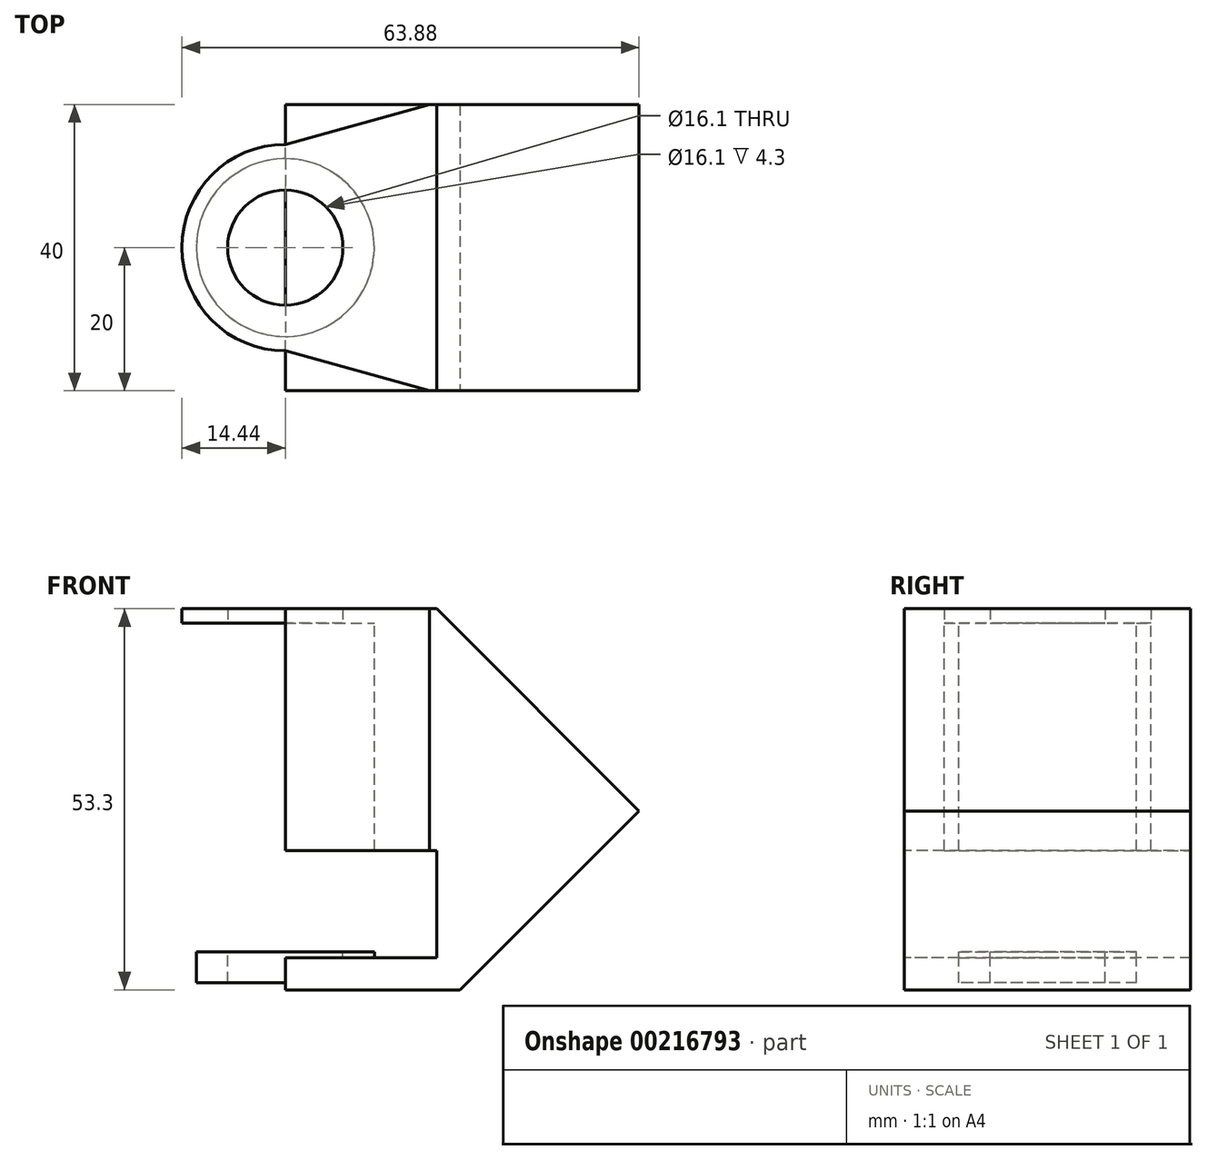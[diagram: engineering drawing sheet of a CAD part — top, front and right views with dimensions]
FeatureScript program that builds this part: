
annotation { "Feature Type Name" : "Feature", "Feature Type Description" : "" }
export const myFeature = defineFeature(function(context is Context, id is Id, definition is map)
    precondition{}
    {
        {
            var Q0;
            Q0=qCreatedBy(makeId("Top.planeOp"),FACE);
            var sketch = newSketch(context, id + "F0", { "sketchPlane" : qUnion([Q0])});
            skCircle(sketch, "E0", {"center": v(0, 0) * mm, "radius": 12.44 * mm});
            skCircle(sketch, "E1", {"center": v(0, 0) * mm, "radius": 8.05 * mm});
            skLineSegment(sketch, "E2", {"start": v(20.16, 20) * mm, "end": v(20.16, -20) * mm});
            skPoint(sketch, "E3", {"position": v(20.16, 0) * mm});
            skCircle(sketch, "E4.0", {"center": v(0, 0) * mm, "radius": 14.44 * mm});
            skFitSpline(sketch, "E5", {"points": [v(0, 14.44) * mm, v(20.16, 20) * mm], "startDerivative": vector(20.16, 5.56) * mm, "endDerivative": vector(20.16, 5.56) * mm});
            skFitSpline(sketch, "E6", {"points": [v(0, -14.44) * mm, v(20.16, -20) * mm], "startDerivative": vector(20.16, -5.56) * mm, "endDerivative": vector(20.16, -5.56) * mm});
            skLineSegment(sketch, "E7", {"start": v(0, -14.44) * mm, "end": v(0, 14.44) * mm});
            skSolve(sketch);
        }
        {
            var Q0;
            {var subQ0=sQuery(id+"F0.wireOp",EDGE,"E7");var subQ1=sQuery(id+"F0.wireOp",EDGE,"E0");var subQ2=makeQuery(id+"F0.imprint","INTERSECT",VERTEX,{"disambiguationData":[OD(0.0)],"derivedFrom":[subQ1,subQ0]});Q0=makeQuery(id+"F0.imprint","IMPRINT",FACE,{"disambiguationData":[TD([[makeQuery(id+"F0.imprint","IMPRINT",EDGE,{"disambiguationData":[TD([[subQ2,-1.0]])],"derivedFrom":subQ1}),-1.0]])]});}
            extrude(context, id + "F1", {"entities" : qUnion([Q0]), "oppositeDirection" : true, "depth" : 31.8 * mm});
        }
        {
            var Q0;
            Q0=makeQuery(id+"F0.imprint","IMPRINT",FACE,{"disambiguationData":[TD([[makeQuery(id+"F0.imprint","IMPRINT",EDGE,{"derivedFrom":sQuery(id+"F0.wireOp",EDGE,"E2")}),-1.0]])]});
            extrude(context, id + "F2", {"entities" : qUnion([Q0]), "operationType" : NewBodyOperationType.ADD, "oppositeDirection" : true, "depth" : 31.8 * mm});
        }
        {
            var Q0;
            {var subQ0=sQuery(id+"F0.wireOp",EDGE,"E7");var subQ1=sQuery(id+"F0.wireOp",EDGE,"E0");var subQ2=makeQuery(id+"F0.imprint","INTERSECT",VERTEX,{"disambiguationData":[OD(0.0)],"derivedFrom":[subQ1,subQ0]});Q0=makeQuery(id+"F0.imprint","IMPRINT",FACE,{"disambiguationData":[TD([[makeQuery(id+"F0.imprint","IMPRINT",EDGE,{"disambiguationData":[TD([[subQ2,1.0]])],"derivedFrom":subQ1}),-1.0]])]});}
            var Q1;
            {var subQ0=sQuery(id+"F0.wireOp",EDGE,"E7");var subQ1=sQuery(id+"F0.wireOp",EDGE,"E0");var subQ2=makeQuery(id+"F0.imprint","INTERSECT",VERTEX,{"disambiguationData":[OD(0.0)],"derivedFrom":[subQ1,subQ0]});Q1=makeQuery(id+"F0.imprint","IMPRINT",FACE,{"disambiguationData":[TD([[makeQuery(id+"F0.imprint","IMPRINT",EDGE,{"disambiguationData":[TD([[subQ2,1.0]])],"derivedFrom":subQ1}),1.0]])]});}
            var Q2;
            {var subQ0=sQuery(id+"F0.wireOp",EDGE,"E7");var subQ1=sQuery(id+"F0.wireOp",EDGE,"E0");var subQ2=makeQuery(id+"F0.imprint","INTERSECT",VERTEX,{"disambiguationData":[OD(0.0)],"derivedFrom":[subQ1,subQ0]});Q2=makeQuery(id+"F0.imprint","IMPRINT",FACE,{"disambiguationData":[TD([[makeQuery(id+"F0.imprint","IMPRINT",EDGE,{"disambiguationData":[TD([[subQ2,-1.0]])],"derivedFrom":subQ1}),1.0]])]});}
            var Q3;
            {var subQ0=sQuery(id+"F0.wireOp",EDGE,"E7");var subQ1=sQuery(id+"F0.wireOp",EDGE,"E0");var subQ2=makeQuery(id+"F0.imprint","INTERSECT",VERTEX,{"disambiguationData":[OD(0.0)],"derivedFrom":[subQ1,subQ0]});Q3=makeQuery(id+"F0.imprint","IMPRINT",FACE,{"disambiguationData":[TD([[makeQuery(id+"F0.imprint","IMPRINT",EDGE,{"disambiguationData":[TD([[subQ2,-1.0]])],"derivedFrom":subQ1}),-1.0]])]});}
            var Q4;
            Q4=makeQuery(id+"F0.imprint","IMPRINT",FACE,{"disambiguationData":[TD([[makeQuery(id+"F0.imprint","IMPRINT",EDGE,{"derivedFrom":sQuery(id+"F0.wireOp",EDGE,"E2")}),-1.0]])]});
            extrude(context, id + "F3", {"entities" : qUnion([Q0, Q1, Q2, Q3, Q4]), "operationType" : NewBodyOperationType.ADD, "depth" : 2 * mm});
        }
        {
            var Q0;
            {var subQ0=sQuery(id+"F0.wireOp",EDGE,"E2");Q0=makeQuery(id+"F3.boolean.opBoolean","MERGE",FACE,{"derivedFrom":[makeQuery(id+"F2.opExtrude","SWEPT_FACE",FACE,{"disambiguationData":[OSD([subQ0])]}),makeQuery(id+"F3.opExtrude","SWEPT_FACE",FACE,{"disambiguationData":[OSD([subQ0])]})]});}
            extrude(context, id + "F4", {"entities" : qUnion([Q0]), "operationType" : NewBodyOperationType.ADD, "depth" : 1 * mm});
        }
        {
            var Q0;
            Q0=makeQuery(id+"F4.opExtrude","SWEPT_FACE",FACE,{"disambiguationData":[OSD([sQuery(id+"F0.wireOp",EDGE,"E2"),sQuery(id+"F0.wireOp",EDGE,"E6")])]});
            var sketch = newSketch(context, id + "F5", { "sketchPlane" : qUnion([Q0])});
            skLineSegment(sketch, "E8", {"start": v(21.16, 2) * mm, "end": v(49.44, -26.28) * mm});
            skLineSegment(sketch, "E9", {"start": v(49.44, -26.28) * mm, "end": v(24.42, -51.3) * mm});
            skLineSegment(sketch, "E10", {"start": v(21.16, -46.8) * mm, "end": v(21.16, -31.8) * mm});
            skLineSegment(sketch, "E11", {"start": v(24.42, -51.3) * mm, "end": v(0, -51.3) * mm});
            skLineSegment(sketch, "E12", {"start": v(21.16, -46.8) * mm, "end": v(0, -46.8) * mm});
            skLineSegment(sketch, "E13", {"start": v(0, -46.8) * mm, "end": v(0, -51.3) * mm});
            skSolve(sketch);
        }
        {
            var Q0;
            {var subQ0=sQuery(id+"F0.wireOp",EDGE,"E7");var subQ1=sQuery(id+"F0.wireOp",EDGE,"E0");var subQ2=makeQuery(id+"F0.imprint","INTERSECT",VERTEX,{"disambiguationData":[OD(0.0)],"derivedFrom":[subQ1,subQ0]});Q0=makeQuery(id+"F0.imprint","IMPRINT",FACE,{"disambiguationData":[TD([[makeQuery(id+"F0.imprint","IMPRINT",EDGE,{"disambiguationData":[TD([[subQ2,1.0]])],"derivedFrom":subQ1}),1.0]])]});}
            var Q1;
            {var subQ0=sQuery(id+"F0.wireOp",EDGE,"E7");var subQ1=sQuery(id+"F0.wireOp",EDGE,"E0");var subQ2=makeQuery(id+"F0.imprint","INTERSECT",VERTEX,{"disambiguationData":[OD(0.0)],"derivedFrom":[subQ1,subQ0]});Q1=makeQuery(id+"F0.imprint","IMPRINT",FACE,{"disambiguationData":[TD([[makeQuery(id+"F0.imprint","IMPRINT",EDGE,{"disambiguationData":[TD([[subQ2,-1.0]])],"derivedFrom":subQ1}),1.0]])]});}
            extrude(context, id + "F6", {"entities" : qUnion([Q0, Q1]), "oppositeDirection" : true, "depth" : 50.3 * mm, "hasSecondDirection" : true, "secondDirectionOppositeDirection" : true, "secondDirectionDepth" : 46 * mm});
        }
        {
            var Q0;
            Q0=makeQuery(id+"F5.imprint","IMPRINT",FACE,{"disambiguationData":[TD([[makeQuery(id+"F5.imprint","IMPRINT",EDGE,{"derivedFrom":sQuery(id+"F5.wireOp",EDGE,"E8")}),-1.0]])]});
            var Q1;
            Q1=makeQuery(id+"F4.opExtrude","SWEPT_FACE",FACE,{"disambiguationData":[OSD([sQuery(id+"F0.wireOp",EDGE,"E2"),sQuery(id+"F0.wireOp",EDGE,"E5")])]});
            extrude(context, id + "F7", {"entities" : qUnion([Q0]), "operationType" : NewBodyOperationType.ADD, "endBound" : BoundingType.UP_TO_SURFACE, "oppositeDirection" : true, "endBoundEntityFace" : qUnion([Q1]), "depth" : 25 * mm});
        }
    });
